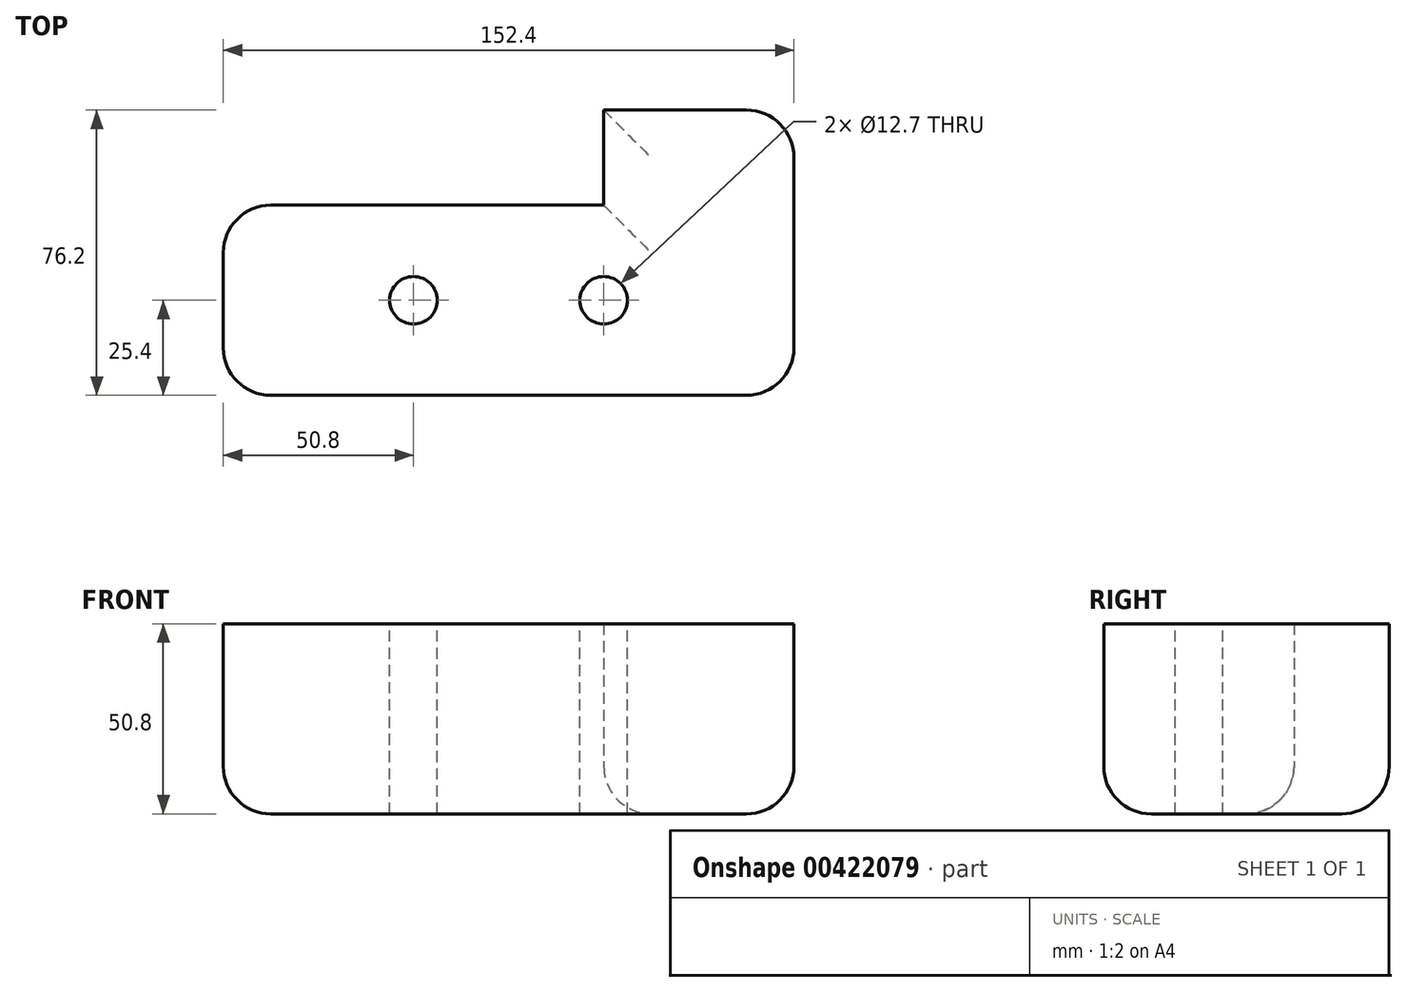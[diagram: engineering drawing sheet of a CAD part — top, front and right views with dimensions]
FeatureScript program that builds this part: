
annotation { "Feature Type Name" : "Feature", "Feature Type Description" : "" }
export const myFeature = defineFeature(function(context is Context, id is Id, definition is map)
    precondition{}
    {
        {
            var Q0;
            Q0=qCreatedBy(makeId("Top.planeOp"),FACE);
            var sketch = newSketch(context, id + "F0", { "sketchPlane" : qUnion([Q0])});
            skLineSegment(sketch, "E0", {"start": v(0, 0) * mm, "end": v(152.4, 0) * mm});
            skLineSegment(sketch, "E1", {"start": v(0, 0) * mm, "end": v(0, 50.8) * mm});
            skLineSegment(sketch, "E2", {"start": v(0, 50.8) * mm, "end": v(101.6, 50.8) * mm});
            skLineSegment(sketch, "E3", {"start": v(101.6, 50.8) * mm, "end": v(101.6, 76.2) * mm});
            skLineSegment(sketch, "E4", {"start": v(101.6, 76.2) * mm, "end": v(152.4, 76.2) * mm});
            skLineSegment(sketch, "E5", {"start": v(152.4, 76.2) * mm, "end": v(152.4, 0) * mm});
            skSolve(sketch);
        }
        {
            var Q0;
            Q0=makeQuery(id+"F0.imprint","IMPRINT",FACE,{"disambiguationData":[TD([[makeQuery(id+"F0.imprint","IMPRINT",EDGE,{"derivedFrom":sQuery(id+"F0.wireOp",EDGE,"E0")}),1.0]])]});
            extrude(context, id + "F1", {"entities" : qUnion([Q0]), "depth" : 50.8 * mm});
        }
        {
            var Q0;
            Q0=makeQuery(id+"F1.opExtrude","CAP_FACE",FACE,{"disambiguationData":[OSD([sQuery(id+"F0.wireOp",EDGE,"E0"),sQuery(id+"F0.wireOp",EDGE,"E1"),sQuery(id+"F0.wireOp",EDGE,"E2"),sQuery(id+"F0.wireOp",EDGE,"E3"),sQuery(id+"F0.wireOp",EDGE,"E4"),sQuery(id+"F0.wireOp",EDGE,"E5")])],"isStart":true});
            var Q1;
            Q1=makeQuery(id+"F1.opExtrude","SWEPT_EDGE",EDGE,{"disambiguationData":[OSD([sQuery(id+"F0.wireOp",EDGE,"E0"),sQuery(id+"F0.wireOp",EDGE,"E5")])]});
            var Q2;
            Q2=makeQuery(id+"F1.opExtrude","SWEPT_EDGE",EDGE,{"disambiguationData":[OSD([sQuery(id+"F0.wireOp",EDGE,"E0"),sQuery(id+"F0.wireOp",EDGE,"E1")])]});
            var Q3;
            Q3=makeQuery(id+"F1.opExtrude","SWEPT_EDGE",EDGE,{"disambiguationData":[OSD([sQuery(id+"F0.wireOp",EDGE,"E1"),sQuery(id+"F0.wireOp",EDGE,"E2")])]});
            var Q4;
            Q4=makeQuery(id+"F1.opExtrude","SWEPT_EDGE",EDGE,{"disambiguationData":[OSD([sQuery(id+"F0.wireOp",EDGE,"E4"),sQuery(id+"F0.wireOp",EDGE,"E5")])]});
            fillet(context, id + "F2", {"entities" : qUnion([Q0, Q1, Q2, Q3, Q4]), "radius" : 12.7 * mm, "tangentPropagation" : true, "allowEdgeOverflow" : false});
        }
        {
            var Q0;
            Q0=makeQuery(id+"F1.opExtrude","CAP_FACE",FACE,{"disambiguationData":[OSD([sQuery(id+"F0.wireOp",EDGE,"E0"),sQuery(id+"F0.wireOp",EDGE,"E1"),sQuery(id+"F0.wireOp",EDGE,"E2"),sQuery(id+"F0.wireOp",EDGE,"E3"),sQuery(id+"F0.wireOp",EDGE,"E4"),sQuery(id+"F0.wireOp",EDGE,"E5")])],"isStart":false});
            var sketch = newSketch(context, id + "F3", { "sketchPlane" : qUnion([Q0])});
            skPoint(sketch, "E6", {"position": v(0, 25.4) * mm});
            skPoint(sketch, "E7", {"position": v(50.8, 25.4) * mm});
            skPoint(sketch, "E8", {"position": v(101.6, 25.4) * mm});
            skSolve(sketch);
        }
        {
            var Q0;
            Q0=sQuery(id+"F3.wireOp",VERTEX,"E7");
            var Q1;
            Q1=sQuery(id+"F3.wireOp",VERTEX,"E8");
            var Q2;
            Q2=makeQuery(id+"F1.opExtrude","SWEPT_BODY",BODY,{"disambiguationData":[OSD([sQuery(id+"F0.wireOp",EDGE,"E0"),sQuery(id+"F0.wireOp",EDGE,"E1"),sQuery(id+"F0.wireOp",EDGE,"E2"),sQuery(id+"F0.wireOp",EDGE,"E3"),sQuery(id+"F0.wireOp",EDGE,"E4"),sQuery(id+"F0.wireOp",EDGE,"E5")])]});
            hole(context, id + "F4", {"style" : HoleStyle.SIMPLE, "endStyle" : HoleEndStyle.THROUGH, "holeDiameter" : 12.7 * mm, "isTappedThrough" : true, "tappedDepth" : 12.7 * mm, "tapClearance" : 3, "locations" : qUnion([Q0, Q1]), "scope" : qUnion([Q2])});
        }
    });
